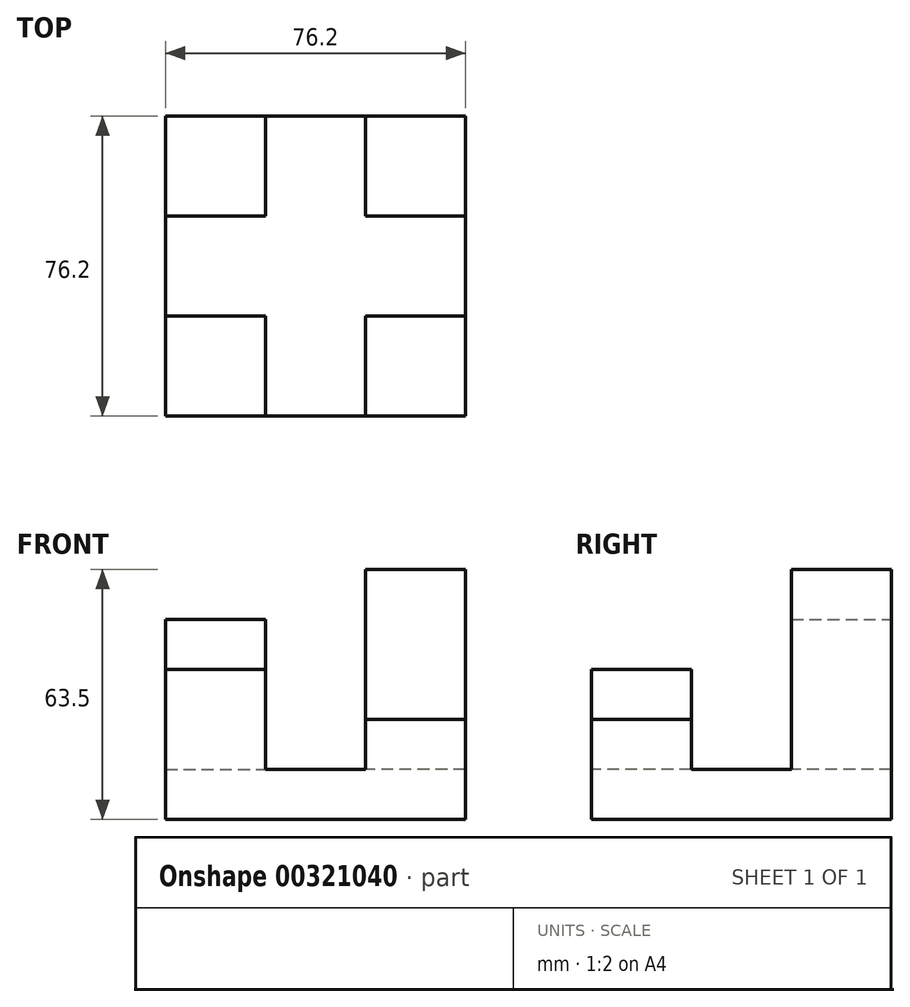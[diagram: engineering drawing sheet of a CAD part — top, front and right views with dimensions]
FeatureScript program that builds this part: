
annotation { "Feature Type Name" : "Feature", "Feature Type Description" : "" }
export const myFeature = defineFeature(function(context is Context, id is Id, definition is map)
    precondition{}
    {
        {
            var Q0;
            Q0=qCreatedBy(makeId("Front.planeOp"),FACE);
            var sketch = newSketch(context, id + "F0", { "sketchPlane" : qUnion([Q0])});
            skLineSegment(sketch, "E0", {"start": v(-39.86, -40.7) * mm, "end": v(36.34, -40.7) * mm});
            skLineSegment(sketch, "E1", {"start": v(36.34, -40.7) * mm, "end": v(36.34, -28) * mm});
            skLineSegment(sketch, "E2", {"start": v(36.34, -28) * mm, "end": v(-39.86, -28) * mm});
            skLineSegment(sketch, "E3", {"start": v(-39.86, -28) * mm, "end": v(-39.86, -40.7) * mm});
            skSolve(sketch);
        }
        {
            var Q0;
            Q0=makeQuery(id+"F0.imprint","IMPRINT",FACE,{"disambiguationData":[TD([[makeQuery(id+"F0.imprint","IMPRINT",EDGE,{"derivedFrom":sQuery(id+"F0.wireOp",EDGE,"E0")}),1.0]])]});
            extrude(context, id + "F1", {"entities" : qUnion([Q0]), "depth" : 76.2 * mm});
        }
        {
            var Q0;
            Q0=makeQuery(id+"F1.opExtrude","SWEPT_FACE",FACE,{"disambiguationData":[OSD([sQuery(id+"F0.wireOp",EDGE,"E2")])]});
            var sketch = newSketch(context, id + "F2", { "sketchPlane" : qUnion([Q0])});
            skLineSegment(sketch, "E4", {"start": v(-39.86, -76.2) * mm, "end": v(-39.86, -50.8) * mm});
            skLineSegment(sketch, "E5", {"start": v(-39.86, -50.8) * mm, "end": v(-14.46, -50.8) * mm});
            skLineSegment(sketch, "E6", {"start": v(-14.46, -50.8) * mm, "end": v(-14.46, -76.2) * mm});
            skLineSegment(sketch, "E7", {"start": v(-14.46, -76.2) * mm, "end": v(-39.86, -76.2) * mm});
            skLineSegment(sketch, "E8.bottom", {"start": v(-39.86, 0) * mm, "end": v(-14.46, 0) * mm});
            skLineSegment(sketch, "E8.top", {"start": v(-39.86, -25.4) * mm, "end": v(-14.46, -25.4) * mm});
            skLineSegment(sketch, "E8.left", {"start": v(-39.86, 0) * mm, "end": v(-39.86, -25.4) * mm});
            skLineSegment(sketch, "E8.right", {"start": v(-14.46, 0) * mm, "end": v(-14.46, -25.4) * mm});
            skLineSegment(sketch, "E9.bottom", {"start": v(36.34, 0) * mm, "end": v(10.94, 0) * mm});
            skLineSegment(sketch, "E9.top", {"start": v(36.34, -25.4) * mm, "end": v(10.94, -25.4) * mm});
            skLineSegment(sketch, "E9.left", {"start": v(36.34, 0) * mm, "end": v(36.34, -25.4) * mm});
            skLineSegment(sketch, "E9.right", {"start": v(10.94, 0) * mm, "end": v(10.94, -25.4) * mm});
            skLineSegment(sketch, "E10.bottom", {"start": v(36.34, -76.2) * mm, "end": v(10.94, -76.2) * mm});
            skLineSegment(sketch, "E10.top", {"start": v(36.34, -50.8) * mm, "end": v(10.94, -50.8) * mm});
            skLineSegment(sketch, "E10.left", {"start": v(36.34, -76.2) * mm, "end": v(36.34, -50.8) * mm});
            skLineSegment(sketch, "E10.right", {"start": v(10.94, -76.2) * mm, "end": v(10.94, -50.8) * mm});
            skSolve(sketch);
        }
        {
            var Q0;
            Q0=makeQuery(id+"F2.imprint","IMPRINT",FACE,{"disambiguationData":[TD([[makeQuery(id+"F2.imprint","IMPRINT",EDGE,{"derivedFrom":sQuery(id+"F2.wireOp",EDGE,"E4")}),-1.0]])]});
            extrude(context, id + "F3", {"entities" : qUnion([Q0]), "operationType" : NewBodyOperationType.ADD, "depth" : 25.4 * mm});
        }
        {
            var Q0;
            Q0=makeQuery(id+"F2.imprint","IMPRINT",FACE,{"disambiguationData":[TD([[makeQuery(id+"F2.imprint","IMPRINT",EDGE,{"derivedFrom":sQuery(id+"F2.wireOp",EDGE,"E10.bottom")}),-1.0]])]});
            extrude(context, id + "F4", {"entities" : qUnion([Q0]), "operationType" : NewBodyOperationType.ADD, "depth" : 12.7 * mm});
        }
        {
            var Q0;
            Q0=makeQuery(id+"F2.imprint","IMPRINT",FACE,{"disambiguationData":[TD([[makeQuery(id+"F2.imprint","IMPRINT",EDGE,{"derivedFrom":sQuery(id+"F2.wireOp",EDGE,"E8.bottom")}),1.0]])]});
            extrude(context, id + "F5", {"entities" : qUnion([Q0]), "operationType" : NewBodyOperationType.ADD, "depth" : 38.1 * mm});
        }
        {
            var Q0;
            Q0=makeQuery(id+"F2.imprint","IMPRINT",FACE,{"disambiguationData":[TD([[makeQuery(id+"F2.imprint","IMPRINT",EDGE,{"derivedFrom":sQuery(id+"F2.wireOp",EDGE,"E9.bottom")}),1.0]])]});
            extrude(context, id + "F6", {"entities" : qUnion([Q0]), "operationType" : NewBodyOperationType.ADD, "depth" : 50.8 * mm});
        }
    });
